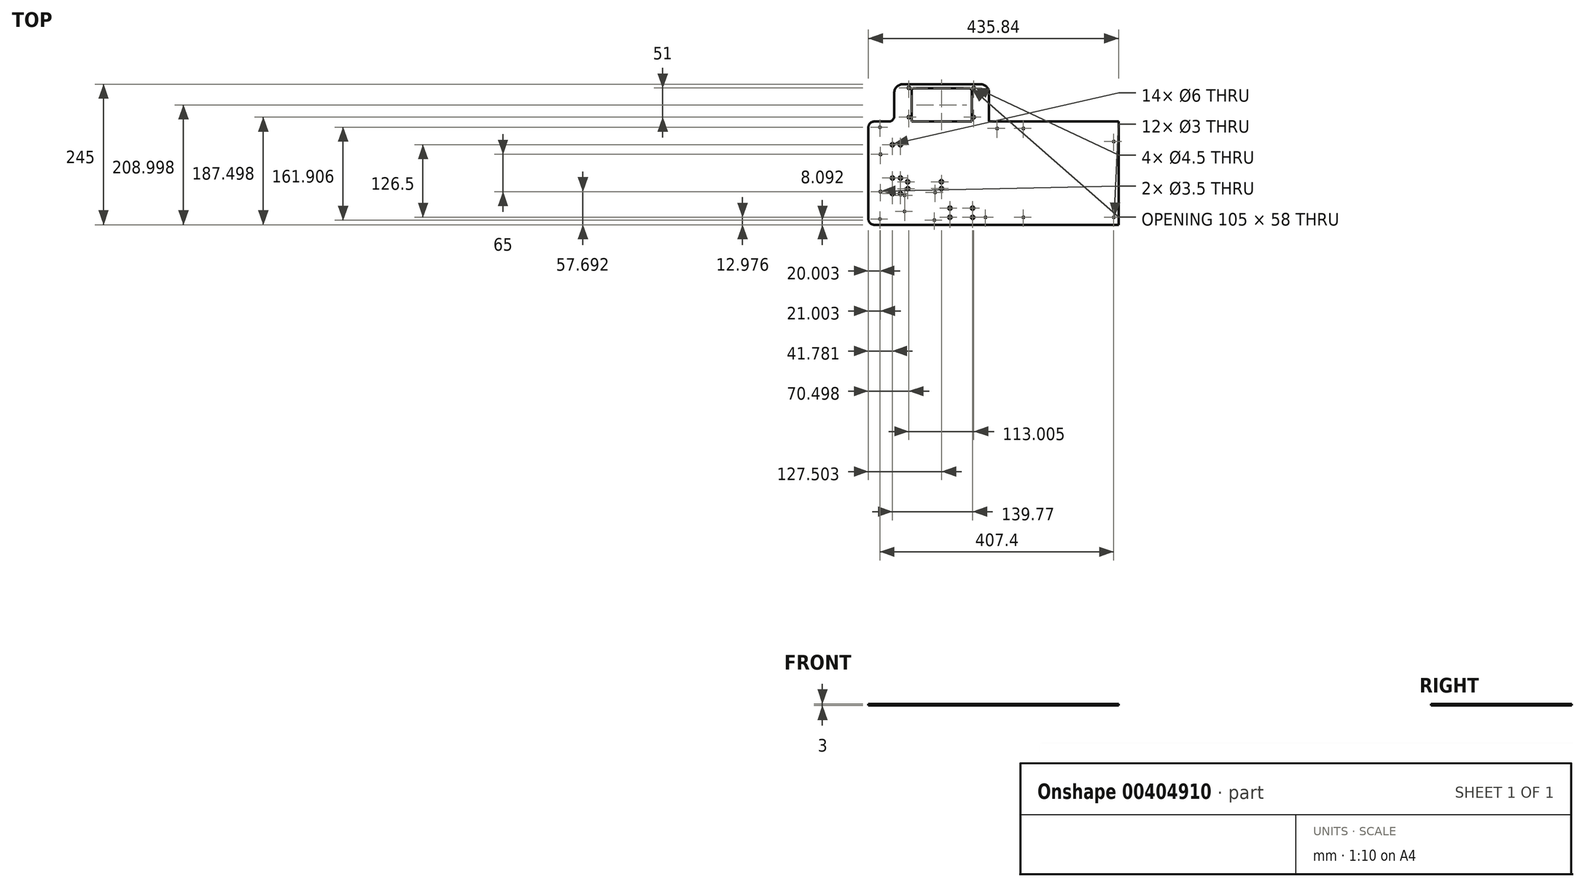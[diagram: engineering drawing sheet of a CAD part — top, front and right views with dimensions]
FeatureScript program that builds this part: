
annotation { "Feature Type Name" : "Feature", "Feature Type Description" : "" }
export const myFeature = defineFeature(function(context is Context, id is Id, definition is map)
    precondition{}
    {
        {
            var Q0;
            Q0=qCreatedBy(makeId("Top.planeOp"),FACE);
            var sketch = newSketch(context, id + "F0", { "sketchPlane" : qUnion([Q0])});
            skLineSegment(sketch, "E0.bottom", {"start": v(-143.53, 58.95) * mm, "end": v(292.31, 58.95) * mm});
            skLineSegment(sketch, "E0.top", {"start": v(-143.53, -121.05) * mm, "end": v(292.31, -121.05) * mm});
            skLineSegment(sketch, "E0.left", {"start": v(-143.53, 58.95) * mm, "end": v(-143.53, -121.05) * mm});
            skLineSegment(sketch, "E0.right", {"start": v(292.31, 58.95) * mm, "end": v(292.31, -121.05) * mm});
            skCircle(sketch, "E1", {"center": v(80.67, 46.79) * mm, "radius": 1.5 * mm});
            skCircle(sketch, "E2", {"center": v(126.4, 46.79) * mm, "radius": 1.5 * mm});
            skCircle(sketch, "E3", {"center": v(283.87, 23.94) * mm, "radius": 1.5 * mm});
            skCircle(sketch, "E4", {"center": v(283.87, -108.05) * mm, "radius": 1.5 * mm});
            skCircle(sketch, "E5", {"center": v(60.35, -108.05) * mm, "radius": 1.5 * mm});
            skCircle(sketch, "E6", {"center": v(126.4, -108.05) * mm, "radius": 1.5 * mm});
            skCircle(sketch, "E7", {"center": v(-27.4, -64.76) * mm, "radius": 1.5 * mm});
            skCircle(sketch, "E8", {"center": v(-28.7, -112.96) * mm, "radius": 1.5 * mm});
            skCircle(sketch, "E9", {"center": v(-80.5, -69.86) * mm, "radius": 1.5 * mm});
            skCircle(sketch, "E10", {"center": v(-80.5, -97.76) * mm, "radius": 1.5 * mm});
            skCircle(sketch, "E11", {"center": v(-122.53, 1.64) * mm, "radius": 1.75 * mm});
            skCircle(sketch, "E12", {"center": v(-122.53, -63.36) * mm, "radius": 1.75 * mm});
            skCircle(sketch, "E13", {"center": v(-123.53, 48.95) * mm, "radius": 1.5 * mm});
            skCircle(sketch, "E14", {"center": v(-123.53, -111.05) * mm, "radius": 1.5 * mm});
            skLineSegment(sketch, "E15.bottom", {"start": v(-82.53, 58.95) * mm, "end": v(66.47, 58.95) * mm});
            skLineSegment(sketch, "E15.top", {"start": v(-82.53, 123.95) * mm, "end": v(51.47, 123.95) * mm});
            skLineSegment(sketch, "E15.right", {"start": v(66.47, 58.95) * mm, "end": v(66.47, 108.95) * mm});
            skLineSegment(sketch, "E16.bottom", {"start": v(-61.05, 58.95) * mm, "end": v(37.07, 58.95) * mm});
            skLineSegment(sketch, "E16.top", {"start": v(-63.53, 116.95) * mm, "end": v(31.47, 116.95) * mm});
            skLineSegment(sketch, "E17", {"start": v(-68.53, 111.95) * mm, "end": v(-68.53, 58.95) * mm});
            skLineSegment(sketch, "E18", {"start": v(-68.53, 58.95) * mm, "end": v(36.47, 58.95) * mm});
            skLineSegment(sketch, "E19", {"start": v(36.47, 58.95) * mm, "end": v(36.47, 111.95) * mm});
            skLineSegment(sketch, "E20", {"start": v(-82.53, 123.95) * mm, "end": v(-83.53, 123.95) * mm});
            skLineSegment(sketch, "E21", {"start": v(-98.53, 108.95) * mm, "end": v(-98.53, 58.95) * mm});
            skPoint(sketch, "E22.visualSharp", {"position": v(-68.53, 116.95) * mm});
            skArc(sketch, "E22.filletArc", {"start": v(-63.53, 116.95) * mm, "mid": v(-67.06, 115.48) * mm, "end": v(-68.53, 111.95) * mm});
            skPoint(sketch, "E23.visualSharp", {"position": v(36.47, 116.95) * mm});
            skArc(sketch, "E23.filletArc", {"start": v(36.47, 111.95) * mm, "mid": v(35, 115.48) * mm, "end": v(31.47, 116.95) * mm});
            skPoint(sketch, "E24.visualSharp", {"position": v(-98.53, 123.95) * mm});
            skArc(sketch, "E24.filletArc", {"start": v(-83.53, 123.95) * mm, "mid": v(-94.13, 119.55) * mm, "end": v(-98.53, 108.95) * mm});
            skPoint(sketch, "E25.visualSharp", {"position": v(66.47, 123.95) * mm});
            skArc(sketch, "E25.filletArc", {"start": v(66.47, 108.95) * mm, "mid": v(62.08, 119.55) * mm, "end": v(51.47, 123.95) * mm});
            skCircle(sketch, "E26", {"center": v(39.97, 66.45) * mm, "radius": 2.25 * mm});
            skCircle(sketch, "E27", {"center": v(-73.03, 66.45) * mm, "radius": 2.25 * mm});
            skCircle(sketch, "E28", {"center": v(-73.03, 117.45) * mm, "radius": 2.25 * mm});
            skCircle(sketch, "E29", {"center": v(39.97, 117.45) * mm, "radius": 2.25 * mm});
            skLineSegment(sketch, "E30", {"start": v(39.96, 58.95) * mm, "end": v(39.96, 123.95) * mm, "construction": true});
            skCircle(sketch, "E31", {"center": v(-101.75, 18.43) * mm, "radius": 3 * mm});
            skCircle(sketch, "E32", {"center": v(-87.75, 18.4) * mm, "radius": 3 * mm});
            skCircle(sketch, "E33", {"center": v(-101.71, -39.6) * mm, "radius": 3 * mm});
            skCircle(sketch, "E34", {"center": v(-87.71, -39.63) * mm, "radius": 3 * mm});
            skCircle(sketch, "E35", {"center": v(-101.62, -66.78) * mm, "radius": 3 * mm});
            skCircle(sketch, "E36", {"center": v(-87.62, -66.8) * mm, "radius": 3 * mm});
            skCircle(sketch, "E37", {"center": v(-75.14, -46.13) * mm, "radius": 3 * mm});
            skCircle(sketch, "E38", {"center": v(-75.1, -58.13) * mm, "radius": 3 * mm});
            skCircle(sketch, "E39", {"center": v(-16.4, -46.05) * mm, "radius": 3 * mm});
            skCircle(sketch, "E40", {"center": v(-16.35, -58.05) * mm, "radius": 3 * mm});
            skCircle(sketch, "E41", {"center": v(37.98, -92.07) * mm, "radius": 3 * mm});
            skCircle(sketch, "E42", {"center": v(38.02, -108.07) * mm, "radius": 3 * mm});
            skCircle(sketch, "E43", {"center": v(-1.51, -92.03) * mm, "radius": 3 * mm});
            skCircle(sketch, "E44", {"center": v(-1.47, -108.03) * mm, "radius": 3 * mm});
            skSolve(sketch);
        }
        {
            var Q0;
            Q0 = qSketchRegion(id + "F0", true);
            extrude(context, id + "F1", {"entities" : qUnion([Q0]), "depth" : 3 * mm});
        }
        {
            var Q0;
            Q0=makeQuery(id+"F1.opExtrude","SWEPT_EDGE",EDGE,{"disambiguationData":[OSD([sQuery(id+"F0.wireOp",EDGE,"E0.bottom"),sQuery(id+"F0.wireOp",EDGE,"E21")])]});
            var Q1;
            Q1=makeQuery(id+"F1.opExtrude","SWEPT_EDGE",EDGE,{"disambiguationData":[OSD([sQuery(id+"F0.wireOp",EDGE,"E0.top"),sQuery(id+"F0.wireOp",EDGE,"E0.left")])]});
            var Q2;
            Q2=makeQuery(id+"F1.opExtrude","SWEPT_EDGE",EDGE,{"disambiguationData":[OSD([sQuery(id+"F0.wireOp",EDGE,"E0.bottom"),sQuery(id+"F0.wireOp",EDGE,"E0.left")])]});
            fillet(context, id + "F2", {"entities" : qUnion([Q0, Q1, Q2]), "radius" : 10 * mm, "tangentPropagation" : true, "allowEdgeOverflow" : false});
        }
    });
